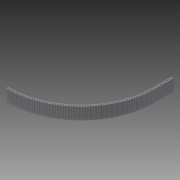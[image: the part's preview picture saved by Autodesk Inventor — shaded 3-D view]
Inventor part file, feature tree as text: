
AUTODESK INVENTOR PART (.ipt)
format: ipt  version: 2013 (Build 170138000, 138)  size: 247,296 bytes
history: native  units: in
note: dims shown in document units (in); Inventor stores cm internally (conversion verified against a paired STEP export)
features: extrude x3, sketch x3
ambient origin geometry x8: Origin, YZ Plane, XZ Plane, XY Plane, X Axis, Y Axis, Z Axis, Center Point
bodies: Solid1 (feature_tree)
feature tree (6):
  extrude  "Extrusion1"  Depth=28.0in
  extrude  "Extrusion5"  Depth=2.5in TaperAngle=0.0deg
  extrude  "Extrusion9"  Depth=4.5in
  sketch  "Sketch1"  dims[d0=8.0in d2=28.0in]
  sketch  "Sketch5"  dims[d5=11.0in d7=2.5in d8=0.0in]
  sketch  "Sketch11"  dims[d46=0.925in d47=0.425in d67=4.5in d89=0.925in d93=0.5in d94=0.266in d95=0.25in d96=0.266in d97=0.266in d98=0.25in d99=0.25in d100=0.25in d101=0.25in d102=0.25in d103=4.0in d104=25.0in d105=4.0in d106=3.1496in d108=0.4688in d109=0.3937in d111=1.0in d113=3.937in d115=0.375in d116=0.3937in d118=1.0in d120=23.622in d122=90.0deg d124=2.5in d125=0.0in d142=3.75in d143=100.0in d144=0.0in]
